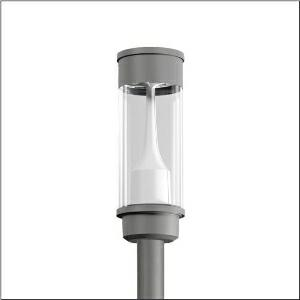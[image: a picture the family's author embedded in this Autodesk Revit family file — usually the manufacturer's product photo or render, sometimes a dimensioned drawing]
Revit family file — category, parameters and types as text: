
# Revit family: litepole_iq___st1_2a_5xa5415af14h_245c
name_source: partatom
category: Lighting Fixtures
units: mm (PartAtom-declared; Revit-internal decimal feet)

## family parameters
Cut with Voids When Loaded = No
Host = Face
Light Source = No
Part Type = Normal
Room Calculation Point = No
Round Connector Dimension = Use Diameter
Shared = No

## types (1)
- --- (1 x LED, 1540 lm, 12.9 W, 2200K)
    Apparent Load = 13 VA
    CIE Flux Codes = 22 61 93 96 100
    Color Rendering = 70
    Color Temperature = 2200K
    Default Elevation = 1800 mm
    Description = Litepole iQ, mast luminaire, Module 540 iQ-SR, primary light control with 3 zone facetted reflector, of plastic, silver coated, highly specular, structured, primary optical cover: cover, of PMMA, transparent, partly coated, light distribution: ST1.2a, light emission: direct distribution, primary light characteristic: asymmetric, installation type: post-top, LED, High Power LED, rated luminous flux: 1.540lm, luminous efficacy: 119lm/W, light colour: 722, colour temperature: 2200K, control gear: iQ Street-Remote, control: optimised constant luminous flux control (CLO 2.0), Desk-Remote (wireless, voltage-free reading and setting of iQ features in the workshop via application-optimized NFC function/RFID function), Light-Fading, Smart-Wire, Night-Set, Lumen-Switch, Temp-Guard, Auto-Match, Street-Remote, pre-setting: logarithmic dimming characteristic, with terminal, 6-pole, max. 2.5mm², mains connection: 230..240V, AC, 50/60Hz, start of lifetime: 13W, end of service life: 13W, reduction: 6W, luminaire housing, upper part, of glass-fibre reinforced polyester, coated, Siteco® metallic grey (DB 702S), diameter: 210mm, height: 590mm, spigot size: d x l = 76 x 70mm (post-top) | with reducer (optional accessory) 60 x 70mm, mounting height: 3..5m, post-top mast mounting element, of diecast aluminium, coated, Siteco® metallic grey (DB 702S), Module 540 iQ-SR, traffic white (RAL 9016), equipment: standard, protection rating (complete): IP65, insulation class (complete): insulation class II (safety insulation), certification: CE, ENEC, VDE, packaging unit: 1 piece

Light Distribution: ST1.2a
    Height = 590 mm
    Lamp = 1 x LED
    Lamp Light Flux = 1540 lm
    Lamp Power = 12.9 W
    Lamp count = 1
    Length = 220 mm
    Luminous efficacy = 119 lm/W
    Manufacturer = Siteco
    ModVariant = No
    Model = 5XA5415AF14H
    Number of Poles = 1
    OnlyDefault = Yes
    Power Factor = 1
    Product Name = Litepole iQ | ST1.2a
    Product group = mast luminaire | pylon top
    ProductGroupID = 6100
    Protection Class = Protection class II
    Protection Degree = IP 65
    RLX_Detail_Level = 1
    RLX_Emergency_Light_Flux = 0 lm
    RLX_Emergency_Type = 0
    RLX_Emergency_Type_DB = No
    RlxData = <blob elided: 72369 chars, md5=028eec6a>
    Socket = socket
    Standby Power = 0 W
    System Light Flux = 1540 lm
    System Power = 13 W
    Type Comments = factory setting: luminous flux: 100 % | dim-lin: 254 | 516 mA
    Type Image = l_1006025.jpg
    URL = http://relux.com
    VarID = @adj_158369
    Voltage = 0 V
    Weight = 0.00 kg
    Width = 0 mm  [stored 0 ft]

note: [stored X ft] marks values corroborated as IEEE doubles in the binary element streams (Revit-internal decimal feet)

## geometry (parser evidence)
native form markers: Blend x4, Sweep x11
no freeform markers — native parametric forms only
